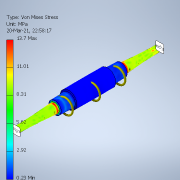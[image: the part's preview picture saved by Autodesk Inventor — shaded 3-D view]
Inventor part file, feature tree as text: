
AUTODESK INVENTOR PART (.ipt)
format: ipt  version: 2021 (Build 250183000, 183)  size: 148,992 bytes
history: native  units: in
note: dims shown in document units (in); Inventor stores cm internally (conversion verified against a paired STEP export)
features: extrude x3, sketch x3, mirror x1
ambient origin geometry x8: Origin, YZ Plane, XZ Plane, XY Plane, X Axis, Y Axis, Z Axis, Center Point
bodies: Solid1 (feature_tree)
feature tree (7):
  extrude  "Extrusion1"  Depth=39.3701in TaperAngle=0.0deg
  extrude  "Extrusion2"  Depth=27.5591in TaperAngle=0.0deg
  extrude  "Extrusion3"  Depth=78.7402in TaperAngle=0.0deg
  mirror  "Mirror1"
  sketch  "Sketch1"  dims[d0=19.685in d1=39.3701in d2=0.0in]
  sketch  "Sketch2"  dims[d3=15.748in d4=27.5591in d5=0.0in]
  sketch  "Sketch3"  dims[d6=11.811in d7=78.7402in d8=0.0in]
